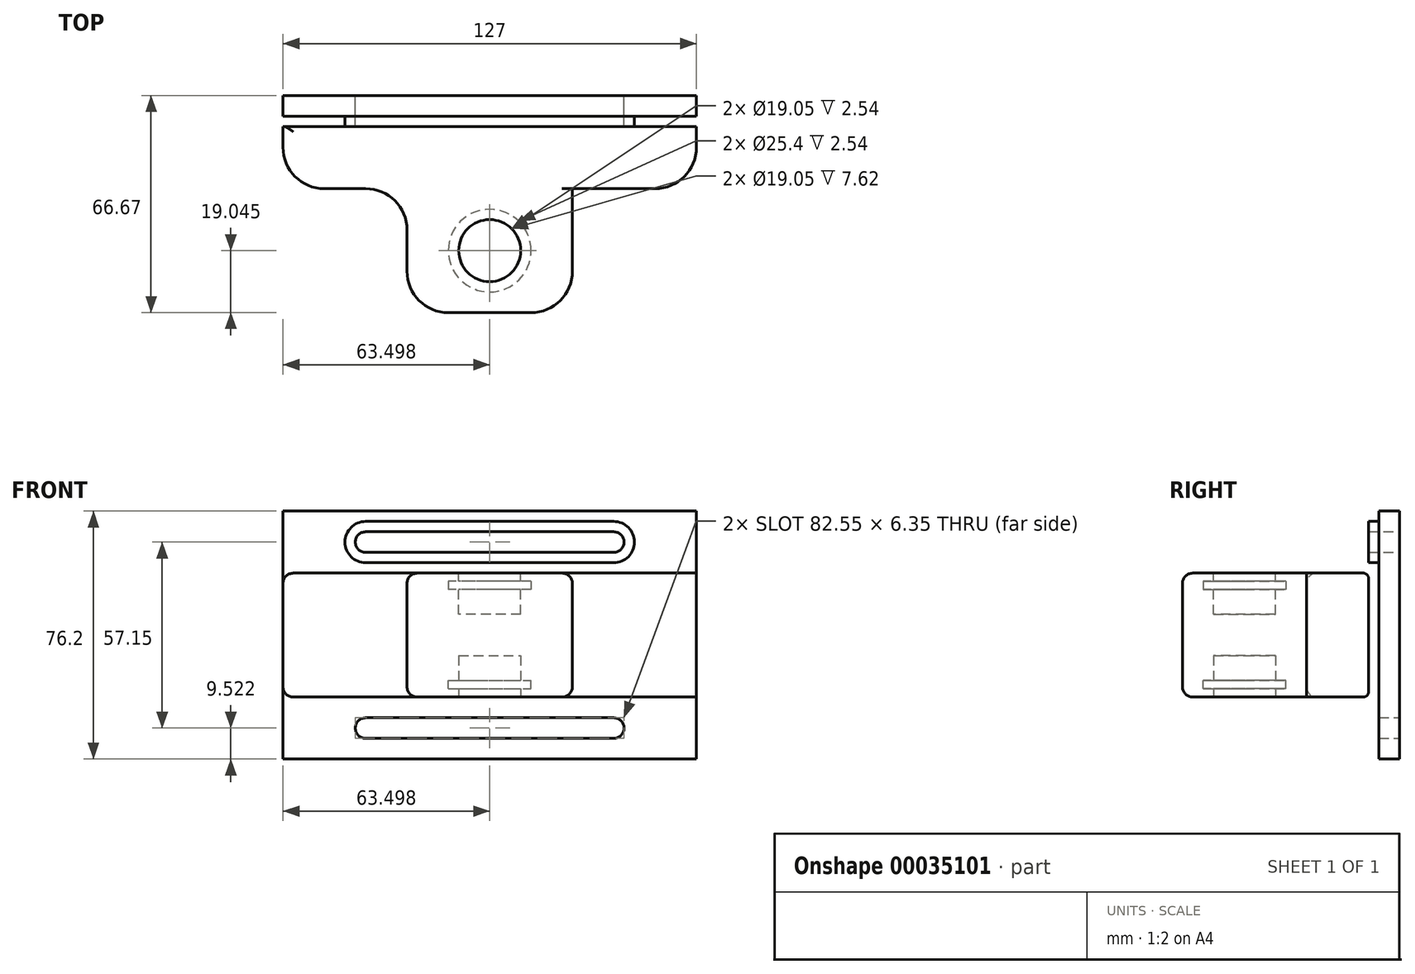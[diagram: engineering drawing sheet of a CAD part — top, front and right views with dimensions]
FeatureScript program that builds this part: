
annotation { "Feature Type Name" : "Feature", "Feature Type Description" : "" }
export const myFeature = defineFeature(function(context is Context, id is Id, definition is map)
    precondition{}
    {
        {
            var Q0;
            Q0=qCreatedBy(makeId("Front.planeOp"),FACE);
            var sketch = newSketch(context, id + "F0", { "sketchPlane" : qUnion([Q0])});
            skLineSegment(sketch, "E0.bottom", {"start": v(-69, 44.47) * mm, "end": v(58, 44.47) * mm});
            skLineSegment(sketch, "E0.top", {"start": v(-69, -31.73) * mm, "end": v(58, -31.73) * mm});
            skLineSegment(sketch, "E0.left", {"start": v(-69, 44.47) * mm, "end": v(-69, -31.73) * mm});
            skLineSegment(sketch, "E0.right", {"start": v(58, 44.47) * mm, "end": v(58, -31.73) * mm});
            skArc(sketch, "E1", {"start": v(-43.6, -19.03) * mm, "mid": v(-46.77, -22.2) * mm, "end": v(-43.6, -25.38) * mm});
            skArc(sketch, "E2", {"start": v(32.6, -25.38) * mm, "mid": v(35.78, -22.2) * mm, "end": v(32.6, -19.03) * mm});
            skLineSegment(sketch, "E3", {"start": v(-43.6, -19.03) * mm, "end": v(32.6, -19.03) * mm});
            skLineSegment(sketch, "E4", {"start": v(-43.6, -25.38) * mm, "end": v(32.6, -25.38) * mm});
            skLineSegment(sketch, "E5", {"start": v(58, 6.37) * mm, "end": v(-69, 6.37) * mm, "construction": true});
            skArc(sketch, "E6.MirrorCS", {"start": v(-43.6, 31.77) * mm, "mid": v(-46.77, 34.94) * mm, "end": v(-43.6, 38.12) * mm});
            skLineSegment(sketch, "E7.MirrorCS", {"start": v(-43.6, 31.77) * mm, "end": v(32.6, 31.77) * mm});
            skArc(sketch, "E8.MirrorCS", {"start": v(32.6, 38.12) * mm, "mid": v(35.78, 34.94) * mm, "end": v(32.6, 31.77) * mm});
            skLineSegment(sketch, "E9.MirrorCS", {"start": v(-43.6, 38.12) * mm, "end": v(32.6, 38.12) * mm});
            skSolve(sketch);
        }
        {
            var Q0;
            Q0=makeQuery(id+"F0.imprint","IMPRINT",FACE,{"disambiguationData":[TD([[makeQuery(id+"F0.imprint","IMPRINT",EDGE,{"derivedFrom":sQuery(id+"F0.wireOp",EDGE,"E0.bottom")}),-1.0]])]});
            extrude(context, id + "F1", {"entities" : qUnion([Q0]), "depth" : 9.52 * mm});
        }
        {
            var Q0;
            Q0=makeQuery(id+"F1.opExtrude","CAP_FACE",FACE,{"disambiguationData":[OSD([sQuery(id+"F0.wireOp",EDGE,"E0.bottom"),sQuery(id+"F0.wireOp",EDGE,"E0.top"),sQuery(id+"F0.wireOp",EDGE,"E0.left"),sQuery(id+"F0.wireOp",EDGE,"E0.right"),sQuery(id+"F0.wireOp",EDGE,"E1"),sQuery(id+"F0.wireOp",EDGE,"E2"),sQuery(id+"F0.wireOp",EDGE,"E3"),sQuery(id+"F0.wireOp",EDGE,"E4"),sQuery(id+"F0.wireOp",EDGE,"E6.MirrorCS"),sQuery(id+"F0.wireOp",EDGE,"E7.MirrorCS"),sQuery(id+"F0.wireOp",EDGE,"E8.MirrorCS"),sQuery(id+"F0.wireOp",EDGE,"E9.MirrorCS")])],"isStart":false});
            var sketch = newSketch(context, id + "F2", { "sketchPlane" : qUnion([Q0])});
            skArc(sketch, "E10", {"start": v(-43.6, -15.86) * mm, "mid": v(-49.94, -22.2) * mm, "end": v(-43.6, -28.56) * mm});
            skArc(sketch, "E11", {"start": v(32.6, -28.56) * mm, "mid": v(38.96, -22.2) * mm, "end": v(32.6, -15.86) * mm});
            skLineSegment(sketch, "E12", {"start": v(-43.6, -15.86) * mm, "end": v(32.6, -15.86) * mm});
            skLineSegment(sketch, "E13", {"start": v(-43.6, -28.56) * mm, "end": v(32.6, -28.56) * mm});
            skLineSegment(sketch, "E14", {"start": v(-69, 6.37) * mm, "end": v(58, 6.37) * mm, "construction": true});
            skArc(sketch, "E15.MirrorCS", {"start": v(-43.6, 28.6) * mm, "mid": v(-49.94, 34.94) * mm, "end": v(-43.6, 41.3) * mm});
            skLineSegment(sketch, "E16.MirrorCS", {"start": v(-43.6, 28.6) * mm, "end": v(32.6, 28.6) * mm});
            skArc(sketch, "E17.MirrorCS", {"start": v(32.6, 41.3) * mm, "mid": v(38.96, 34.94) * mm, "end": v(32.6, 28.6) * mm});
            skLineSegment(sketch, "E18.MirrorCS", {"start": v(-43.6, 41.3) * mm, "end": v(32.6, 41.3) * mm});
            skSolve(sketch);
        }
        {
            var Q0;
            Q0=makeQuery(id+"F2.imprint","IMPRINT",FACE,{"disambiguationData":[TD([[makeQuery(id+"F2.imprint","IMPRINT",EDGE,{"derivedFrom":sQuery(id+"F2.wireOp",EDGE,"E15.MirrorCS")}),-1.0]])]});
            var Q1;
            Q1=makeQuery(id+"F2.imprint","IMPRINT",FACE,{"disambiguationData":[TD([[makeQuery(id+"F2.imprint","IMPRINT",EDGE,{"derivedFrom":sQuery(id+"F2.wireOp",EDGE,"E10")}),1.0]])]});
            extrude(context, id + "F3", {"entities" : qUnion([Q0, Q1]), "operationType" : NewBodyOperationType.REMOVE, "oppositeDirection" : true, "depth" : 3.17 * mm});
        }
        {
            var Q0;
            Q0=makeQuery(id+"F1.opExtrude","CAP_FACE",FACE,{"disambiguationData":[OSD([sQuery(id+"F0.wireOp",EDGE,"E0.bottom"),sQuery(id+"F0.wireOp",EDGE,"E0.top"),sQuery(id+"F0.wireOp",EDGE,"E0.left"),sQuery(id+"F0.wireOp",EDGE,"E0.right"),sQuery(id+"F0.wireOp",EDGE,"E1"),sQuery(id+"F0.wireOp",EDGE,"E2"),sQuery(id+"F0.wireOp",EDGE,"E3"),sQuery(id+"F0.wireOp",EDGE,"E4"),sQuery(id+"F0.wireOp",EDGE,"E6.MirrorCS"),sQuery(id+"F0.wireOp",EDGE,"E7.MirrorCS"),sQuery(id+"F0.wireOp",EDGE,"E8.MirrorCS"),sQuery(id+"F0.wireOp",EDGE,"E9.MirrorCS")])],"isStart":false});
            var sketch = newSketch(context, id + "F4", { "sketchPlane" : qUnion([Q0])});
            skLineSegment(sketch, "E19.bottom", {"start": v(-69, -12.68) * mm, "end": v(58, -12.68) * mm});
            skLineSegment(sketch, "E19.top", {"start": v(-69, 25.42) * mm, "end": v(58, 25.42) * mm});
            skLineSegment(sketch, "E19.left", {"start": v(-69, -12.68) * mm, "end": v(-69, 25.42) * mm});
            skLineSegment(sketch, "E19.right", {"start": v(58, -12.68) * mm, "end": v(58, 25.42) * mm});
            skSolve(sketch);
        }
        {
            var Q0;
            Q0=makeQuery(id+"F4.imprint","IMPRINT",FACE,{"disambiguationData":[TD([[makeQuery(id+"F4.imprint","IMPRINT",EDGE,{"derivedFrom":sQuery(id+"F4.wireOp",EDGE,"E19.bottom")}),1.0]])]});
            extrude(context, id + "F5", {"entities" : qUnion([Q0]), "operationType" : NewBodyOperationType.ADD, "depth" : 19.05 * mm});
        }
        {
            var Q0;
            Q0=makeQuery(id+"F5.opExtrude","CAP_FACE",FACE,{"disambiguationData":[OSD([sQuery(id+"F4.wireOp",EDGE,"E19.bottom"),sQuery(id+"F4.wireOp",EDGE,"E19.top"),sQuery(id+"F4.wireOp",EDGE,"E19.left"),sQuery(id+"F4.wireOp",EDGE,"E19.right")])],"isStart":false});
            var sketch = newSketch(context, id + "F6", { "sketchPlane" : qUnion([Q0])});
            skLineSegment(sketch, "E20.bottom", {"start": v(-30.9, -12.68) * mm, "end": v(19.9, -12.68) * mm});
            skLineSegment(sketch, "E20.top", {"start": v(-30.9, 25.42) * mm, "end": v(19.9, 25.42) * mm});
            skLineSegment(sketch, "E20.left", {"start": v(-30.9, -12.68) * mm, "end": v(-30.9, 25.42) * mm});
            skLineSegment(sketch, "E20.right", {"start": v(19.9, -12.68) * mm, "end": v(19.9, 25.42) * mm});
            skSolve(sketch);
        }
        {
            var Q0;
            Q0=makeQuery(id+"F6.imprint","IMPRINT",FACE,{"disambiguationData":[TD([[makeQuery(id+"F6.imprint","IMPRINT",EDGE,{"derivedFrom":sQuery(id+"F6.wireOp",EDGE,"E20.bottom")}),1.0]])]});
            extrude(context, id + "F7", {"entities" : qUnion([Q0]), "operationType" : NewBodyOperationType.ADD, "depth" : 38.1 * mm});
        }
        {
            var Q0;
            Q0=makeQuery(id+"F7.boolean.opBoolean","MERGE",FACE,{"derivedFrom":[makeQuery(id+"F5.opExtrude","SWEPT_FACE",FACE,{"disambiguationData":[OSD([sQuery(id+"F4.wireOp",EDGE,"E19.bottom")])]}),makeQuery(id+"F7.opExtrude","SWEPT_FACE",FACE,{"disambiguationData":[OSD([sQuery(id+"F6.wireOp",EDGE,"E20.bottom")])]})]});
            var sketch = newSketch(context, id + "F8", { "sketchPlane" : qUnion([Q0])});
            skPoint(sketch, "E21", {"position": v(-5.5, 47.63) * mm});
            skSolve(sketch);
        }
        {
            var Q0;
            Q0=sQuery(id+"F8.wireOp",VERTEX,"E21");
            var Q1;
            Q1=makeQuery(id+"F1.opExtrude","SWEPT_BODY",BODY,{"disambiguationData":[OSD([sQuery(id+"F0.wireOp",EDGE,"E0.bottom"),sQuery(id+"F0.wireOp",EDGE,"E0.top"),sQuery(id+"F0.wireOp",EDGE,"E0.left"),sQuery(id+"F0.wireOp",EDGE,"E0.right"),sQuery(id+"F0.wireOp",EDGE,"E1"),sQuery(id+"F0.wireOp",EDGE,"E2"),sQuery(id+"F0.wireOp",EDGE,"E3"),sQuery(id+"F0.wireOp",EDGE,"E4"),sQuery(id+"F0.wireOp",EDGE,"E6.MirrorCS"),sQuery(id+"F0.wireOp",EDGE,"E7.MirrorCS"),sQuery(id+"F0.wireOp",EDGE,"E8.MirrorCS"),sQuery(id+"F0.wireOp",EDGE,"E9.MirrorCS")])]});
            hole(context, id + "F9", {"style" : HoleStyle.SIMPLE, "holeDiameter" : 9.52 * mm, "endStyle" : HoleEndStyle.THROUGH, "locations" : qUnion([Q0]), "scope" : qUnion([Q1])});
        }
        {
            var Q0;
            Q0=makeQuery(id+"F7.boolean.opBoolean","MERGE",FACE,{"derivedFrom":[makeQuery(id+"F5.opExtrude","SWEPT_FACE",FACE,{"disambiguationData":[OSD([sQuery(id+"F4.wireOp",EDGE,"E19.bottom")])]}),makeQuery(id+"F7.opExtrude","SWEPT_FACE",FACE,{"disambiguationData":[OSD([sQuery(id+"F6.wireOp",EDGE,"E20.bottom")])]})]});
            var sketch = newSketch(context, id + "F10", { "sketchPlane" : qUnion([Q0])});
            skCircle(sketch, "E22", {"center": v(-5.5, 47.63) * mm, "radius": 9.53 * mm});
            skSolve(sketch);
        }
        {
            var Q0;
            Q0=makeQuery(id+"F10.imprint","IMPRINT",FACE,{"disambiguationData":[TD([[makeQuery(id+"F10.imprint","IMPRINT",EDGE,{"derivedFrom":sQuery(id+"F10.wireOp",EDGE,"E22")}),1.0]])]});
            extrude(context, id + "F11", {"entities" : qUnion([Q0]), "operationType" : NewBodyOperationType.REMOVE, "oppositeDirection" : true, "depth" : 12.7 * mm});
        }
        {
            var Q0;
            Q0=makeQuery(id+"F7.boolean.opBoolean","MERGE",FACE,{"derivedFrom":[makeQuery(id+"F5.opExtrude","SWEPT_FACE",FACE,{"disambiguationData":[OSD([sQuery(id+"F4.wireOp",EDGE,"E19.top")])]}),makeQuery(id+"F7.opExtrude","SWEPT_FACE",FACE,{"disambiguationData":[OSD([sQuery(id+"F6.wireOp",EDGE,"E20.top")])]})]});
            var sketch = newSketch(context, id + "F12", { "sketchPlane" : qUnion([Q0])});
            skCircle(sketch, "E23", {"center": v(-5.5, -47.63) * mm, "radius": 9.53 * mm});
            skSolve(sketch);
        }
        {
            var Q0;
            Q0=makeQuery(id+"F12.imprint","IMPRINT",FACE,{"disambiguationData":[TD([[makeQuery(id+"F12.imprint","IMPRINT",EDGE,{"derivedFrom":sQuery(id+"F12.wireOp",EDGE,"E23")}),1.0]])]});
            extrude(context, id + "F13", {"entities" : qUnion([Q0]), "operationType" : NewBodyOperationType.REMOVE, "oppositeDirection" : true, "depth" : 12.7 * mm});
        }
        {
            var Q0;
            Q0=makeQuery(id+"F1.opExtrude","SWEPT_FACE",FACE,{"disambiguationData":[OSD([sQuery(id+"F0.wireOp",EDGE,"E0.top")])]});
            cPlane(context, id + "F14", {"entities" : qUnion([Q0]), "cplaneType" : CPlaneType.OFFSET, "offset" : 24.13 * mm, "oppositeDirection" : true, "width" : 152.4 * mm, "height" : 152.4 * mm});
        }
        {
            var Q0;
            Q0=qCreatedBy(id+"F14.planeOp",FACE);
            var sketch = newSketch(context, id + "F15", { "sketchPlane" : qUnion([Q0])});
            skCircle(sketch, "E24", {"center": v(-5.5, 47.63) * mm, "radius": 12.7 * mm});
            skSolve(sketch);
        }
        {
            var Q0;
            Q0=makeQuery(id+"F1.opExtrude","SWEPT_FACE",FACE,{"disambiguationData":[OSD([sQuery(id+"F0.wireOp",EDGE,"E0.bottom")])]});
            cPlane(context, id + "F16", {"entities" : qUnion([Q0]), "cplaneType" : CPlaneType.OFFSET, "offset" : 24.13 * mm, "oppositeDirection" : true, "width" : 152.4 * mm, "height" : 152.4 * mm});
        }
        {
            var Q0;
            Q0=qCreatedBy(id+"F16.planeOp",FACE);
            var sketch = newSketch(context, id + "F17", { "sketchPlane" : qUnion([Q0])});
            skCircle(sketch, "E25.0", {"center": v(-5.5, -47.63) * mm, "radius": 12.7 * mm});
            skSolve(sketch);
        }
        {
            var Q0;
            Q0 = qSketchRegion(id + "F17", true);
            var Q1;
            Q1=makeQuery(id+"F7.boolean.opBoolean","MERGE",FACE,{"derivedFrom":[makeQuery(id+"F5.opExtrude","SWEPT_FACE",FACE,{"disambiguationData":[OSD([sQuery(id+"F4.wireOp",EDGE,"E19.top")])]}),makeQuery(id+"F7.opExtrude","SWEPT_FACE",FACE,{"disambiguationData":[OSD([sQuery(id+"F6.wireOp",EDGE,"E20.top")])]})]});
            extrude(context, id + "F18", {"entities" : qUnion([Q0, Q1]), "operationType" : NewBodyOperationType.REMOVE, "depth" : 2.54 * mm});
        }
        {
            var Q0;
            Q0 = qSketchRegion(id + "F15", true);
            var Q1;
            Q1=makeQuery(id+"F7.boolean.opBoolean","MERGE",FACE,{"derivedFrom":[makeQuery(id+"F5.opExtrude","SWEPT_FACE",FACE,{"disambiguationData":[OSD([sQuery(id+"F4.wireOp",EDGE,"E19.bottom")])]}),makeQuery(id+"F7.opExtrude","SWEPT_FACE",FACE,{"disambiguationData":[OSD([sQuery(id+"F6.wireOp",EDGE,"E20.bottom")])]})]});
            extrude(context, id + "F19", {"entities" : qUnion([Q0, Q1]), "operationType" : NewBodyOperationType.REMOVE, "depth" : 2.54 * mm});
        }
        {
            var Q0;
            Q0=makeQuery(id+"F5.opExtrude","CAP_EDGE",EDGE,{"disambiguationData":[OSD([sQuery(id+"F4.wireOp",EDGE,"E19.left")])],"isStart":false});
            var Q1;
            Q1=makeQuery(id+"F7.opExtrude","CAP_EDGE",EDGE,{"disambiguationData":[OSD([sQuery(id+"F6.wireOp",EDGE,"E20.left")])],"isStart":true});
            var Q2;
            Q2=makeQuery(id+"F7.opExtrude","CAP_EDGE",EDGE,{"disambiguationData":[OSD([sQuery(id+"F6.wireOp",EDGE,"E20.left")])],"isStart":false});
            var Q3;
            Q3=makeQuery(id+"F7.opExtrude","CAP_EDGE",EDGE,{"disambiguationData":[OSD([sQuery(id+"F6.wireOp",EDGE,"E20.right")])],"isStart":false});
            var Q4;
            Q4=makeQuery(id+"F7.opExtrude","CAP_EDGE",EDGE,{"disambiguationData":[OSD([sQuery(id+"F6.wireOp",EDGE,"E20.right")])],"isStart":true});
            var Q5;
            Q5=makeQuery(id+"F5.opExtrude","CAP_EDGE",EDGE,{"disambiguationData":[OSD([sQuery(id+"F4.wireOp",EDGE,"E19.right")])],"isStart":false});
            fillet(context, id + "F20", {"entities" : qUnion([Q0, Q1, Q2, Q3, Q4, Q5]), "radius" : 12.7 * mm, "tangentPropagation" : true, "allowEdgeOverflow" : false});
        }
        {
            var Q0;
            Q0=makeQuery(id+"F5.opExtrude","SWEPT_EDGE",EDGE,{"disambiguationData":[OSD([sQuery(id+"F0.wireOp",EDGE,"E0.left"),sQuery(id+"F4.wireOp",EDGE,"E19.bottom"),sQuery(id+"F4.wireOp",EDGE,"E19.left")])]});
            var Q1;
            {var subQ0=sQuery(id+"F0.wireOp",EDGE,"E0.right");var subQ1=sQuery(id+"F0.wireOp",EDGE,"E0.top");Q1=makeQuery(id+"F5.boolean.opBoolean","SPLIT",EDGE,{"disambiguationData":[TD([makeQuery(id+"F1.opExtrude","SWEPT_FACE",FACE,{"disambiguationData":[OSD([subQ1])]})])],"derivedFrom":makeQuery(id+"F1.opExtrude","CAP_EDGE",EDGE,{"disambiguationData":[OSD([subQ0])],"isStart":false})});}
            var Q2;
            Q2=makeQuery(id+"F1.opExtrude","CAP_EDGE",EDGE,{"disambiguationData":[OSD([sQuery(id+"F0.wireOp",EDGE,"E0.top")])],"isStart":false});
            var Q3;
            {var subQ0=sQuery(id+"F0.wireOp",EDGE,"E0.left");var subQ1=sQuery(id+"F0.wireOp",EDGE,"E0.top");Q3=makeQuery(id+"F5.boolean.opBoolean","SPLIT",EDGE,{"disambiguationData":[TD([makeQuery(id+"F1.opExtrude","SWEPT_FACE",FACE,{"disambiguationData":[OSD([subQ1])]})])],"derivedFrom":makeQuery(id+"F1.opExtrude","CAP_EDGE",EDGE,{"disambiguationData":[OSD([subQ0])],"isStart":false})});}
            var Q4;
            Q4=makeQuery(id+"F5.opExtrude","SWEPT_EDGE",EDGE,{"disambiguationData":[OSD([sQuery(id+"F0.wireOp",EDGE,"E0.left"),sQuery(id+"F4.wireOp",EDGE,"E19.top"),sQuery(id+"F4.wireOp",EDGE,"E19.left")])]});
            var Q5;
            {var subQ0=sQuery(id+"F0.wireOp",EDGE,"E0.left");var subQ1=sQuery(id+"F0.wireOp",EDGE,"E0.bottom");Q5=makeQuery(id+"F5.boolean.opBoolean","SPLIT",EDGE,{"disambiguationData":[TD([makeQuery(id+"F1.opExtrude","SWEPT_FACE",FACE,{"disambiguationData":[OSD([subQ1])]})])],"derivedFrom":makeQuery(id+"F1.opExtrude","CAP_EDGE",EDGE,{"disambiguationData":[OSD([subQ0])],"isStart":false})});}
            var Q6;
            Q6=makeQuery(id+"F1.opExtrude","CAP_EDGE",EDGE,{"disambiguationData":[OSD([sQuery(id+"F0.wireOp",EDGE,"E0.bottom")])],"isStart":false});
            var Q7;
            {var subQ0=sQuery(id+"F0.wireOp",EDGE,"E0.right");var subQ1=sQuery(id+"F0.wireOp",EDGE,"E0.bottom");Q7=makeQuery(id+"F5.boolean.opBoolean","SPLIT",EDGE,{"disambiguationData":[TD([makeQuery(id+"F1.opExtrude","SWEPT_FACE",FACE,{"disambiguationData":[OSD([subQ1])]})])],"derivedFrom":makeQuery(id+"F1.opExtrude","CAP_EDGE",EDGE,{"disambiguationData":[OSD([subQ0])],"isStart":false})});}
            fillet(context, id + "F21", {"entities" : qUnion([Q0, Q1, Q2, Q3, Q4, Q5, Q6, Q7]), "radius" : 3.17 * mm, "tangentPropagation" : true, "allowEdgeOverflow" : false});
        }
        {
            var Q0;
            Q0=makeQuery(id+"F5.opExtrude","CAP_EDGE",EDGE,{"disambiguationData":[OSD([sQuery(id+"F4.wireOp",EDGE,"E19.bottom")])],"isStart":true});
            var Q1;
            Q1=makeQuery(id+"F5.opExtrude","CAP_EDGE",EDGE,{"disambiguationData":[OSD([sQuery(id+"F4.wireOp",EDGE,"E19.top")])],"isStart":true});
            fillet(context, id + "F22", {"entities" : qUnion([Q0, Q1]), "radius" : 1.6 * mm, "allowEdgeOverflow" : false});
        }
    });
